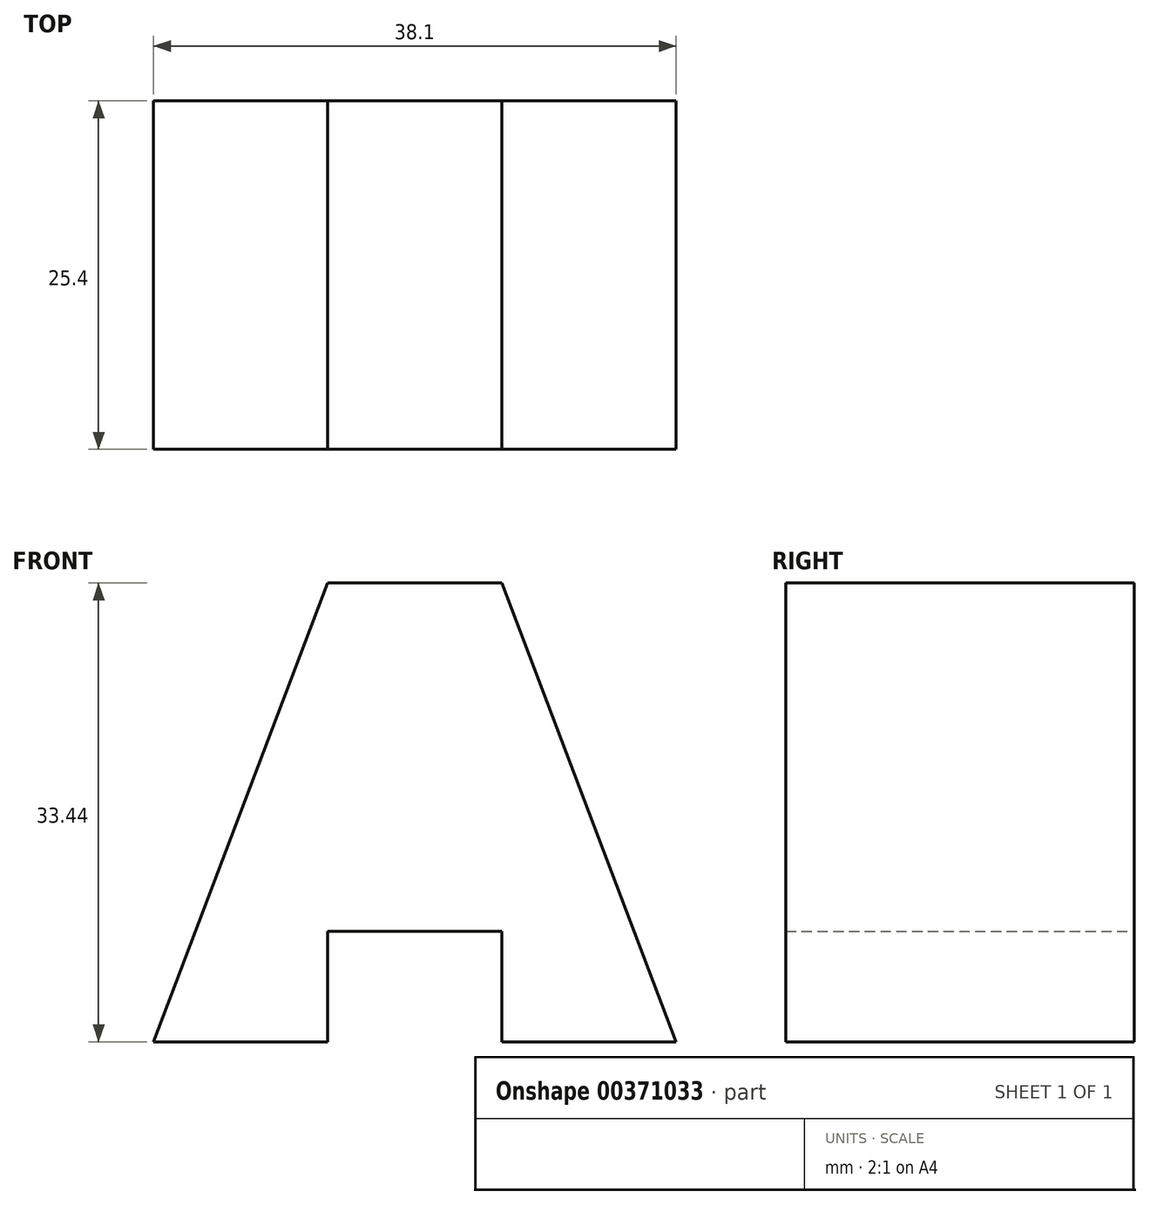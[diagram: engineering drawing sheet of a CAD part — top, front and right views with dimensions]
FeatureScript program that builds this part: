
annotation { "Feature Type Name" : "Feature", "Feature Type Description" : "" }
export const myFeature = defineFeature(function(context is Context, id is Id, definition is map)
    precondition{}
    {
        {
            var Q0;
            Q0=qCreatedBy(makeId("Front.planeOp"),FACE);
            var sketch = newSketch(context, id + "F0", { "sketchPlane" : qUnion([Q0])});
            skLineSegment(sketch, "E0", {"start": v(-19.9, 0) * mm, "end": v(-7.2, 33.44) * mm});
            skLineSegment(sketch, "E1", {"start": v(-7.2, 33.44) * mm, "end": v(5.5, 33.44) * mm});
            skLineSegment(sketch, "E2", {"start": v(5.5, 33.44) * mm, "end": v(18.2, 0) * mm});
            skLineSegment(sketch, "E3", {"start": v(18.2, 0) * mm, "end": v(5.5, 0) * mm});
            skLineSegment(sketch, "E4", {"start": v(5.5, 0) * mm, "end": v(5.5, 8.04) * mm});
            skLineSegment(sketch, "E5", {"start": v(5.5, 8.04) * mm, "end": v(-7.2, 8.04) * mm});
            skLineSegment(sketch, "E6", {"start": v(-7.2, 8.04) * mm, "end": v(-7.2, 0) * mm});
            skLineSegment(sketch, "E7", {"start": v(-19.9, 0) * mm, "end": v(-7.2, 0) * mm});
            skSolve(sketch);
        }
        {
            var Q0;
            Q0=makeQuery(id+"F0.imprint","IMPRINT",FACE,{"disambiguationData":[TD([[makeQuery(id+"F0.imprint","IMPRINT",EDGE,{"derivedFrom":sQuery(id+"F0.wireOp",EDGE,"E0")}),-1.0]])]});
            extrude(context, id + "F1", {"entities" : qUnion([Q0]), "depth" : 25.4 * mm});
        }
    });
